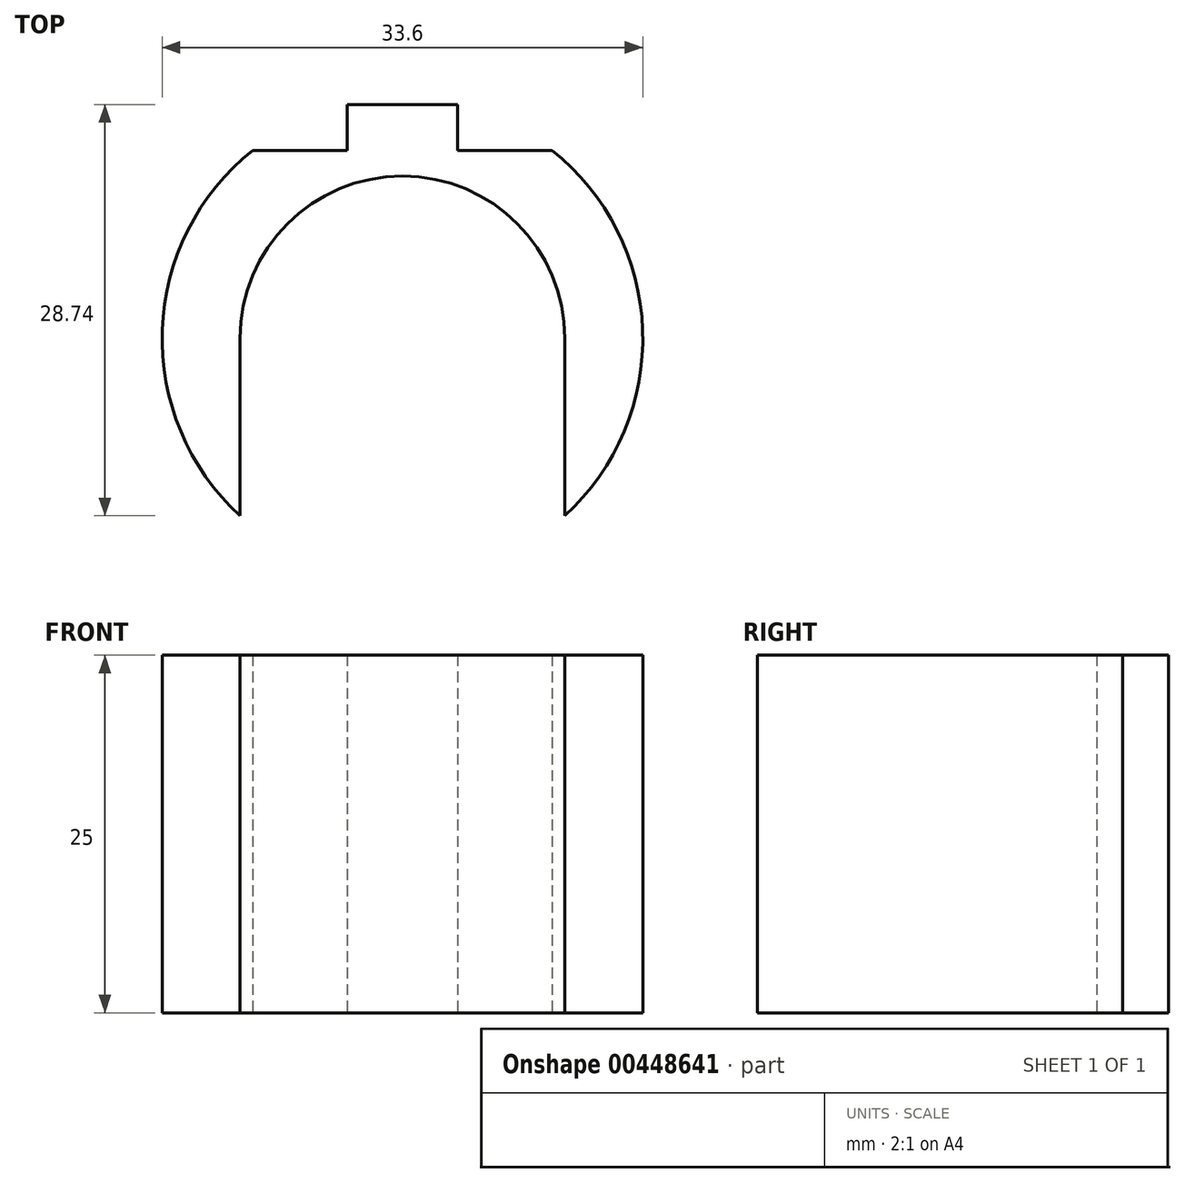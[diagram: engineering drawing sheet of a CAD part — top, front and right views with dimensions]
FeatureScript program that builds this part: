
annotation { "Feature Type Name" : "Feature", "Feature Type Description" : "" }
export const myFeature = defineFeature(function(context is Context, id is Id, definition is map)
    precondition{}
    {
        {
            var Q0;
            Q0=qCreatedBy(makeId("Top.planeOp"),FACE);
            var sketch = newSketch(context, id + "F0", { "sketchPlane" : qUnion([Q0])});
            skCircle(sketch, "E0", {"center": v(0, 0) * mm, "radius": 16.8 * mm});
            skLineSegment(sketch, "E1", {"start": v(0, -16.8) * mm, "end": v(0, 16.8) * mm});
            skLineSegment(sketch, "E2", {"start": v(-3.85, 16.35) * mm, "end": v(3.85, 16.35) * mm});
            skLineSegment(sketch, "E3.top", {"start": v(-3.85, 13.15) * mm, "end": v(3.85, 13.15) * mm});
            skLineSegment(sketch, "E3.left", {"start": v(-3.85, 16.35) * mm, "end": v(-3.85, 13.15) * mm});
            skLineSegment(sketch, "E3.right", {"start": v(3.85, 16.35) * mm, "end": v(3.85, 13.15) * mm});
            skLineSegment(sketch, "E4", {"start": v(-3.85, 13.15) * mm, "end": v(-10.46, 13.15) * mm});
            skLineSegment(sketch, "E5", {"start": v(3.85, 13.15) * mm, "end": v(10.46, 13.15) * mm});
            skCircle(sketch, "E6", {"center": v(0, 0) * mm, "radius": 11.35 * mm});
            skLineSegment(sketch, "E7", {"start": v(-11.35, 0) * mm, "end": v(-11.35, -12.39) * mm});
            skLineSegment(sketch, "E8", {"start": v(11.35, 0) * mm, "end": v(11.35, -12.39) * mm});
            skSolve(sketch);
        }
        {
            var Q0;
            {var subQ0=sQuery(id+"F0.wireOp",EDGE,"E4");Q0=makeQuery(id+"F0.imprint","IMPRINT",FACE,{"disambiguationData":[TD([[makeQuery(id+"F0.imprint","IMPRINT",EDGE,{"derivedFrom":subQ0}),1.0]])]});}
            var Q1;
            {var subQ0=sQuery(id+"F0.wireOp",EDGE,"E5");Q1=makeQuery(id+"F0.imprint","IMPRINT",FACE,{"disambiguationData":[TD([[makeQuery(id+"F0.imprint","IMPRINT",EDGE,{"derivedFrom":subQ0}),-1.0]])]});}
            var Q2;
            {var subQ5=sQuery(id+"F0.wireOp",EDGE,"E3.left");Q2=makeQuery(id+"F0.imprint","IMPRINT",FACE,{"disambiguationData":[TD([[makeQuery(id+"F0.imprint","IMPRINT",EDGE,{"derivedFrom":subQ5}),1.0]])]});}
            var Q3;
            {var subQ5=sQuery(id+"F0.wireOp",EDGE,"E3.right");Q3=makeQuery(id+"F0.imprint","IMPRINT",FACE,{"disambiguationData":[TD([[makeQuery(id+"F0.imprint","IMPRINT",EDGE,{"derivedFrom":subQ5}),-1.0]])]});}
            extrude(context, id + "F1", {"entities" : qUnion([Q0, Q1, Q2, Q3]), "depth" : 25 * mm});
        }
    });
